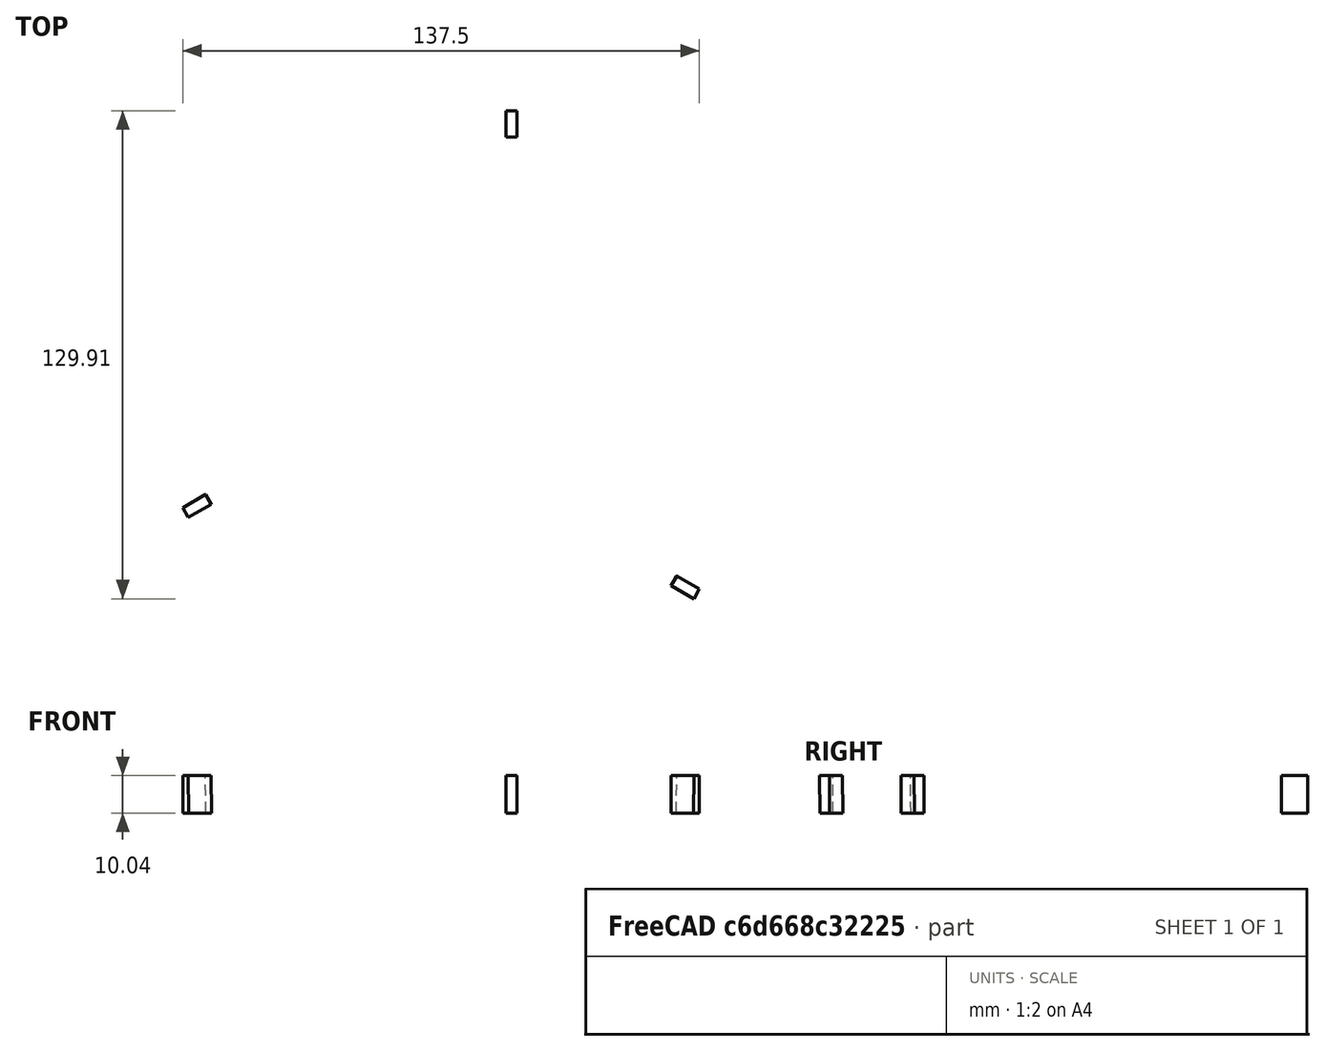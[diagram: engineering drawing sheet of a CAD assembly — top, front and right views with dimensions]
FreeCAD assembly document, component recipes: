
FREECAD ASSEMBLY — COMPONENT RECIPES ("spreadsheet-example-deltarobot")

This assembly document has 17 components, labeled P0..P16 below (a component is one placed body or linked part). 17 of them carry a construction recipe — the FreeCAD feature program that regenerates the part from scratch, quoted from this document or its linked companion documents; the rest are supplied as boundary geometry only. No exploded tour is included for this assembly.
COMPONENT P0 — recipe-attached ("arm", a linked part whose construction recipe lives in a companion FreeCAD document of the same project; that document's serialized recipe follows).
Construction recipe (the companion document, serialized — sketch geometry with constraints, then the solid features built on it; lengths are millimeters unless a unit is written):

FCSTD DOCUMENT  (FreeCAD 2024.1R35694 (Git))
Label: arm
License: All rights reserved
LicenseURL: http://en.wikipedia.org/wiki/All_rights_reserved
objects: Sketcher::SketchObject×11, PartDesign::Pad×6, PartDesign::Plane×2, PartDesign::Revolution×2, PartDesign::Mirrored×2, PartDesign::Body×2, PartDesign::Pocket×2, PartDesign::Chamfer×1, PartDesign::Hole×1, PartDesign::Fillet×1, App::Part×1
note: 43 computed .brp shape members not serialized (recipe doc carries the construction recipe); baked Part::Feature solids carry a one-line shape summary decoded from their .brp

FEATURE [PartDesign::Plane] DatumPlane002  label="midplane001"
  AttachmentOffset = pos=(0,0,7) rot=(0,0,1;0rad)
  Length = 60
  MapMode = 5
  Placement = pos=(0,-7,1.6e-15) rot=(1,0,0;1.5708rad)
  ResizeMode = 0
  Support = -> [XZ_Plane002]
  Width = 60
FEATURE [Sketcher::SketchObject] Sketch008
  FullyConstrained = true
  MapMode = 5
  Placement = pos=(0,0,0) rot=(1,0,0;1.5708rad)
  Support = -> [XZ_Plane002]
  sketch-geometry (5):
    g0: Circle CenterX=0 CenterY=0 CenterZ=0 NormalX=0 NormalY=0 NormalZ=1 AngleXU=0 Radius=2.5
    g1: ArcOfCircle CenterX=0 CenterY=0 CenterZ=0 NormalX=0 NormalY=0 NormalZ=1 AngleXU=0 Radius=6 StartAngle=3.14159 EndAngle=6.28319
    g2: LineSegment StartX=-6 StartY=-1.9e-15 StartZ=0 EndX=-6 EndY=50 EndZ=0
    g3: LineSegment StartX=6 StartY=-1.5e-15 StartZ=0 EndX=6 EndY=50 EndZ=0
    g4: LineSegment StartX=-6 StartY=50 StartZ=0 EndX=6 EndY=50 EndZ=0
  constraints (12):
    c: Coincident(g0,g-1)
    c: Tangent(g1,g2) = 1.5708
    c: Tangent(g1,g3) = -1.5708
    c: Vertical(g3)
    c: Diameter(g0) = 5
    c: Distance(g1,g1) = 12
    c: PointOnObject(g1,g-1)
    c: Coincident(g4,g2)
    c: Coincident(g4,g3)
    c: DistanceY(g3,g3) = 50
    c: Vertical(g2)
    c: Symmetric(g2,g3,g-2)
FEATURE [PartDesign::Pad] Pad003
  Direction = (0,-1,2e-16)
  Length = 8
  Length2 = 10
  Midplane = true
  Placement = pos=(0,0,0) rot=(1,0,0;1.5708rad)
  Profile = -> Sketch008
  ReferenceAxis = -> Sketch008 [N_Axis]
  Type = 0
FEATURE [Sketcher::SketchObject] Sketch009
  FullyConstrained = true
  MapMode = 5
  Placement = pos=(0,0,0) rot=(1,0,0;1.5708rad)
  Support = -> [XZ_Plane002]
  sketch-geometry (2):
    g0: Circle CenterX=0 CenterY=0 CenterZ=0 NormalX=0 NormalY=0 NormalZ=1 AngleXU=0 Radius=2.5
    g1: Circle CenterX=0 CenterY=0 CenterZ=0 NormalX=0 NormalY=0 NormalZ=1 AngleXU=0 Radius=6
  constraints (4):
    c: Coincident(g0,g-1)
    c: Coincident(g1,g0)
    c: Diameter(g0) = 5
    c: Diameter(g1) = 12
FEATURE [PartDesign::Pad] Pad004
  BaseFeature = -> Pad003
  Direction = (0,-1,2e-16)
  Length = 10
  Length2 = 10
  Placement = pos=(0,0,0) rot=(1,0,0;1.5708rad)
  Profile = -> Sketch009
  ReferenceAxis = -> Sketch009 [N_Axis]
  Refine = true
  Type = 0
FEATURE [Sketcher::SketchObject] Sketch010
  ExternalGeometry = -> [Pad004]
  FullyConstrained = true
  MapMode = 5
  Placement = pos=(0,-7,1.6e-15) rot=(1,0,0;1.5708rad)
  Support = -> [DatumPlane002]
  sketch-geometry (4):
    g0: LineSegment StartX=-6 StartY=50 StartZ=0 EndX=6 EndY=50 EndZ=0
    g1: LineSegment StartX=6 StartY=50 StartZ=0 EndX=6 EndY=56 EndZ=0
    g2: LineSegment StartX=6 StartY=56 StartZ=0 EndX=-6 EndY=56 EndZ=0
    g3: LineSegment StartX=-6 StartY=56 StartZ=0 EndX=-6 EndY=50 EndZ=0
  constraints (10):
    c: Coincident(g0,g1)
    c: Coincident(g1,g2)
    c: Coincident(g2,g3)
    c: Coincident(g3,g0)
    c: Horizontal(g2)
    c: Vertical(g1)
    c: Vertical(g3)
    c: Coincident(g0,g-3)
    c: Coincident(g0,g-3)
    c: DistanceY(g1,g1) = 6
FEATURE [PartDesign::Pad] Pad005
  BaseFeature = -> Pad004
  Direction = (0,-1,2e-16)
  Length = 36
  Length2 = 10
  Midplane = true
  Placement = pos=(0,0,0) rot=(1,0,0;1.5708rad)
  Profile = -> Sketch010
  ReferenceAxis = -> Sketch010 [N_Axis]
  Refine = true
  Type = 0
FEATURE [Sketcher::SketchObject] Sketch011
  ExternalGeometry = -> [Pad005,DatumPlane002]
  FullyConstrained = true
  MapMode = 5
  Placement = pos=(0,0,0) rot=(0.57735,0.57735,0.57735;2.0944rad)
  Support = -> [YZ_Plane002]
  sketch-geometry (4):
    g0: LineSegment StartX=-37 StartY=53 StartZ=0 EndX=-25 EndY=53 EndZ=0
    g1: ArcOfCircle CenterX=-32 CenterY=53 CenterZ=0 NormalX=0 NormalY=0 NormalZ=1 AngleXU=0 Radius=5 StartAngle=0.643501 EndAngle=3.14159
    g2: LineSegment StartX=-28 StartY=56 StartZ=0 EndX=-25 EndY=56 EndZ=0
    g3: LineSegment StartX=-25 StartY=56 StartZ=0 EndX=-25 EndY=53 EndZ=0
  constraints (12):
    c: Symmetric(g-3,g-3,g0)
    c: PointOnObject(g1,g0)
    c: Coincident(g1,g0)
    c: PointOnObject(g0,g-3)
    c: Radius(g1) = 5
    c: Distance(g1,g-4) = 25
    c: Coincident(g1,g2)
    c: PointOnObject(g2,g-3)
    c: Horizontal(g2)
    c: Coincident(g2,g3)
    c: Coincident(g3,g0)
    c: DistanceY(g0,g2) = 3
FEATURE [PartDesign::Revolution] Revolution
  Angle = 360
  Angle2 = 60
  Axis = (0,1,0)
  Base = (0,-37,53)
  BaseFeature = -> Pad005
  Placement = pos=(0,0,0) rot=(1,0,0;1.5708rad)
  Profile = -> Sketch011
  ReferenceAxis = -> Sketch011 [Edge1]
  Refine = true
  Type = 0
FEATURE [PartDesign::Mirrored] Mirrored002
  BaseFeature = -> Revolution
  MirrorPlane = -> DatumPlane002
  Originals = -> [Revolution]
  Placement = pos=(0,0,0) rot=(1,0,0;1.5708rad)
  Refine = true
FEATURE [PartDesign::Body] Body001  label="arm-skeleton"
  Group = -> [Sketch008,Pad003,Sketch009,Pad004,DatumPlane002,Sketch010,Pad005,Sketch011,Revolution,Mirrored002]
  Origin = -> Origin002
  Tip = -> Mirrored002
FEATURE [PartDesign::Plane] DatumPlane003  label="midplane002"
  AttachmentOffset = pos=(0,0,7) rot=(0,0,1;0rad)
  Length = 60
  MapMode = 5
  Placement = pos=(0,-7,1.6e-15) rot=(1,0,0;1.5708rad)
  ResizeMode = 0
  Support = -> [XZ_Plane002]
  Width = 60
FEATURE [Sketcher::SketchObject] Sketch012
  FullyConstrained = true
  MapMode = 5
  Placement = pos=(0,0,0) rot=(1,0,0;1.5708rad)
  Support = -> [XZ_Plane003]
  sketch-geometry (5):
    g0: Circle CenterX=0 CenterY=0 CenterZ=0 NormalX=0 NormalY=0 NormalZ=1 AngleXU=0 Radius=2.5
    g1: ArcOfCircle CenterX=0 CenterY=0 CenterZ=0 NormalX=0 NormalY=0 NormalZ=1 AngleXU=0 Radius=6 StartAngle=3.14159 EndAngle=6.28319
    g2: LineSegment StartX=-6 StartY=-1.9e-15 StartZ=0 EndX=-6 EndY=50 EndZ=0
    g3: LineSegment StartX=6 StartY=-1.5e-15 StartZ=0 EndX=6 EndY=50 EndZ=0
    g4: LineSegment StartX=-6 StartY=50 StartZ=0 EndX=6 EndY=50 EndZ=0
  constraints (12):
    c: Coincident(g0,g-1)
    c: Tangent(g1,g2) = 1.5708
    c: Tangent(g1,g3) = -1.5708
    c: Vertical(g3)
    c: Diameter(g0) = 5
    c: Distance(g1,g1) = 12
    c: PointOnObject(g1,g-1)
    c: Coincident(g4,g2)
    c: Coincident(g4,g3)
    c: DistanceY(g3,g3) = 50
    c: Vertical(g2)
    c: Symmetric(g2,g3,g-2)
FEATURE [PartDesign::Pad] Pad006
  Direction = (0,-1,2e-16)
  Length = 8
  Length2 = 10
  Midplane = true
  Placement = pos=(0,0,0) rot=(1,0,0;1.5708rad)
  Profile = -> Sketch012
  ReferenceAxis = -> Sketch012 [N_Axis]
  Type = 0
FEATURE [Sketcher::SketchObject] Sketch013
  FullyConstrained = true
  MapMode = 5
  Placement = pos=(0,0,0) rot=(1,0,0;1.5708rad)
  Support = -> [XZ_Plane003]
  sketch-geometry (2):
    g0: Circle CenterX=0 CenterY=0 CenterZ=0 NormalX=0 NormalY=0 NormalZ=1 AngleXU=0 Radius=2.5
    g1: Circle CenterX=0 CenterY=0 CenterZ=0 NormalX=0 NormalY=0 NormalZ=1 AngleXU=0 Radius=6
  constraints (4):
    c: Coincident(g0,g-1)
    c: Coincident(g1,g0)
    c: Diameter(g0) = 5
    c: Diameter(g1) = 12
FEATURE [PartDesign::Pad] Pad007
  BaseFeature = -> Pad006
  Direction = (0,-1,2e-16)
  Length = 10
  Length2 = 10
  Placement = pos=(0,0,0) rot=(1,0,0;1.5708rad)
  Profile = -> Sketch013
  ReferenceAxis = -> Sketch013 [N_Axis]
  Refine = true
  Type = 0
FEATURE [Sketcher::SketchObject] Sketch014
  ExternalGeometry = -> [Pad007]
  FullyConstrained = true
  MapMode = 5
  Placement = pos=(0,-7,1.6e-15) rot=(1,0,0;1.5708rad)
  Support = -> [DatumPlane003]
  sketch-geometry (4):
    g0: LineSegment StartX=-6 StartY=50 StartZ=0 EndX=6 EndY=50 EndZ=0
    g1: LineSegment StartX=6 StartY=50 StartZ=0 EndX=6 EndY=56 EndZ=0
    g2: LineSegment StartX=6 StartY=56 StartZ=0 EndX=-6 EndY=56 EndZ=0
    g3: LineSegment StartX=-6 StartY=56 StartZ=0 EndX=-6 EndY=50 EndZ=0
  constraints (10):
    c: Coincident(g0,g1)
    c: Coincident(g1,g2)
    c: Coincident(g2,g3)
    c: Coincident(g3,g0)
    c: Horizontal(g2)
    c: Vertical(g1)
    c: Vertical(g3)
    c: Coincident(g0,g-3)
    c: Coincident(g0,g-3)
    c: DistanceY(g1,g1) = 6
FEATURE [PartDesign::Pad] Pad008
  BaseFeature = -> Pad007
  Direction = (0,-1,2e-16)
  Length = 36
  Length2 = 10
  Midplane = true
  Placement = pos=(0,0,0) rot=(1,0,0;1.5708rad)
  Profile = -> Sketch014
  ReferenceAxis = -> Sketch014 [N_Axis]
  Refine = true
  Type = 0
FEATURE [Sketcher::SketchObject] Sketch015
  ExternalGeometry = -> [Pad008,DatumPlane003]
  FullyConstrained = true
  MapMode = 5
  Placement = pos=(0,0,0) rot=(0.57735,0.57735,0.57735;2.0944rad)
  Support = -> [YZ_Plane003]
  sketch-geometry (4):
    g0: LineSegment StartX=-36.9 StartY=53 StartZ=0 EndX=-25 EndY=53 EndZ=0
    g1: ArcOfCircle CenterX=-32 CenterY=53 CenterZ=0 NormalX=0 NormalY=0 NormalZ=1 AngleXU=0 Radius=4.9 StartAngle=0.658897 EndAngle=3.14159
    g2: LineSegment StartX=-28.1257 StartY=56 StartZ=0 EndX=-25 EndY=56 EndZ=0
    g3: LineSegment StartX=-25 StartY=56 StartZ=0 EndX=-25 EndY=53 EndZ=0
  constraints (12):
    c: Symmetric(g-3,g-3,g0)
    c: PointOnObject(g1,g0)
    c: Coincident(g1,g0)
    c: PointOnObject(g0,g-3)
    c: Radius(g1) = 4.9
    c: Distance(g1,g-4) = 25
    c: Coincident(g1,g2)
    c: PointOnObject(g2,g-3)
    c: Horizontal(g2)
    c: Coincident(g2,g3)
    c: Coincident(g3,g0)
    c: DistanceY(g0,g2) = 3
FEATURE [PartDesign::Revolution] Revolution001
  Angle = 360
  Angle2 = 60
  Axis = (0,1,0)
  Base = (0,-36.9,53)
  BaseFeature = -> Pad008
  Placement = pos=(0,0,0) rot=(1,0,0;1.5708rad)
  Profile = -> Sketch015
  ReferenceAxis = -> Sketch015 [Edge1]
  Refine = true
  Type = 0
FEATURE [PartDesign::Mirrored] Mirrored003
  BaseFeature = -> Revolution001
  MirrorPlane = -> DatumPlane003
  Originals = -> [Revolution001]
  Placement = pos=(0,0,0) rot=(1,0,0;1.5708rad)
  Refine = true
FEATURE [PartDesign::Chamfer] Chamfer
  Angle = 45
  Base = -> Mirrored003 [Edge12,Edge10,Edge17,Edge21]
  BaseFeature = -> Mirrored003
  ChamferType = 0
  FlipDirection = false
  Placement = pos=(0,0,0) rot=(1,0,0;1.5708rad)
  Refine = true
  Size = 2
  Size2 = 1
  SupportTransform = false
  UseAllEdges = false
FEATURE [Sketcher::SketchObject] Sketch
  FullyConstrained = true
  MapMode = 5
  Placement = pos=(0,0,0) rot=(1,0,0;1.5708rad)
  Support = -> [XZ_Plane003]
  sketch-geometry (4):
    g0: LineSegment StartX=0.5 StartY=0 StartZ=0 EndX=0.5 EndY=10 EndZ=0
    g1: LineSegment StartX=0.5 StartY=10 StartZ=0 EndX=-0.5 EndY=10 EndZ=0
    g2: LineSegment StartX=-0.5 StartY=10 StartZ=0 EndX=-0.5 EndY=0 EndZ=0
    g3: LineSegment StartX=-0.5 StartY=0 StartZ=0 EndX=0.5 EndY=0 EndZ=0
  constraints (11):
    c: Coincident(g0,g1)
    c: Coincident(g1,g2)
    c: Coincident(g2,g3)
    c: Coincident(g3,g0)
    c: Vertical(g0)
    c: Vertical(g2)
    c: Horizontal(g1)
    c: Horizontal(g3)
    c: Symmetric(g2,g0,g-1)
    c: Distance(g1,g1) = 1
    c: DistanceY(g0,g0) = 10
FEATURE [PartDesign::Pocket] Pocket
  BaseFeature = -> Chamfer
  Direction = (0,1,-2e-16)
  Length = 5
  Length2 = 5
  Midplane = true
  Placement = pos=(0,0,0) rot=(1,0,0;1.5708rad)
  Profile = -> Sketch
  ReferenceAxis = -> Sketch [N_Axis]
  Refine = true
  Type = 1
FEATURE [Sketcher::SketchObject] Sketch016
  FullyConstrained = true
  MapMode = 5
  Placement = pos=(6,0,0) rot=(0.707107,0,0.707107;3.14159rad)
  Support = -> [Pocket]
  sketch-geometry (1):
    g0: Circle CenterX=5 CenterY=0 CenterZ=0 NormalX=0 NormalY=0 NormalZ=1 AngleXU=0 Radius=1.5
  constraints (3):
    c: PointOnObject(g0,g-1)
    c: Diameter(g0) = 3
    c: DistanceX(g-1,g0) = 5
FEATURE [PartDesign::Hole] Hole
  BaseFeature = -> Pocket
  CustomThreadClearance = 0
  Depth = 178.805
  DepthType = 1
  Diameter = 3.4
  DrillForDepth = false
  DrillPoint = 1
  DrillPointAngle = 118
  HoleCutCountersinkAngle = 90
  HoleCutCustomValues = false
  HoleCutDepth = 0
  HoleCutDiameter = 6.1
  HoleCutType = 0
  ModelThread = false
  Placement = pos=(0,0,0) rot=(1,0,0;1.5708rad)
  Profile = -> Sketch016
  Refine = true
  Tapered = false
  TaperedAngle = 90
  ThreadClass = 0
  ThreadDepth = 178.805
  ThreadDepthType = 0
  ThreadDirection = 0
  ThreadFit = 0
  ThreadSize = 9
  ThreadType = 1
  Threaded = false
  UseCustomThreadClearance = false
FEATURE [Sketcher::SketchObject] Sketch017
  ExternalGeometry = -> [Hole]
  FullyConstrained = true
  MapMode = 5
  Placement = pos=(-6,0,0) rot=(0.707107,0,-0.707107;3.14159rad)
  Support = -> [Hole]
  sketch-geometry (7):
    g0: LineSegment StartX=-1.5359 StartY=-4e-16 StartZ=0 EndX=-3.26795 EndY=3 EndZ=0
    g1: LineSegment StartX=-3.26795 StartY=3 StartZ=0 EndX=-6.73205 EndY=3 EndZ=0
    g2: LineSegment StartX=-6.73205 StartY=3 StartZ=0 EndX=-8.4641 EndY=-9e-16 EndZ=0
    g3: LineSegment StartX=-8.4641 StartY=-9e-16 StartZ=0 EndX=-6.73205 EndY=-3 EndZ=0
    g4: LineSegment StartX=-6.73205 StartY=-3 StartZ=0 EndX=-3.26795 EndY=-3 EndZ=0
    g5: LineSegment StartX=-3.26795 StartY=-3 StartZ=0 EndX=-1.5359 EndY=-4e-16 EndZ=0
    g6: Circle CenterX=-5 CenterY=-6e-16 CenterZ=0 NormalX=0 NormalY=0 NormalZ=1 AngleXU=0 Radius=3.4641
  constraints (16):
    c: Coincident(g0,g1)
    c: Coincident(g1,g2)
    c: Coincident(g2,g3)
    c: Coincident(g3,g4)
    c: Coincident(g4,g5)
    c: Coincident(g5,g0)
    c: Equal(g0, g1-g5) x5
    c: PointOnObject(g0,g6)
    c: PointOnObject(g1,g6)
    c: PointOnObject(g2,g6)
    c: PointOnObject(g3,g6)
    c: PointOnObject(g4,g6)
    c: PointOnObject(g5,g6)
    c: Coincident(g6,g-3)
    c: DistanceY(g4,g0) = 6
    c: Horizontal(g1)
FEATURE [PartDesign::Pocket] Pocket001
  BaseFeature = -> Hole
  Direction = (1,0,2e-16)
  Length = 3
  Length2 = 5
  Placement = pos=(0,0,0) rot=(1,0,0;1.5708rad)
  Profile = -> Sketch017
  ReferenceAxis = -> Sketch017 [N_Axis]
  Refine = true
  Type = 0
FEATURE [PartDesign::Fillet] Fillet
  Base = -> Pocket001 [Edge3,Edge46]
  BaseFeature = -> Pocket001
  Placement = pos=(0,0,0) rot=(1,0,0;1.5708rad)
  Radius = 2
  Refine = true
  SupportTransform = false
  UseAllEdges = false
FEATURE [PartDesign::Body] Body002  label="arm0"
  Group = -> [Sketch012,Pad006,Sketch013,Pad007,DatumPlane003,Sketch014,Pad008,Sketch015,Revolution001,Mirrored003,Chamfer,Sketch,Pocket,Sketch016,Hole,Sketch017,Pocket001,Fillet]
  Origin = -> Origin003
  Tip = -> Fillet
FEATURE [App::Part] Part  label="arm"
  Group = -> [Body001,Body002]
  Origin = -> Origin
COMPONENT P1 — same part as P0; its construction recipe is shown at P0.
COMPONENT P2 — same part as P0; its construction recipe is shown at P0.
COMPONENT P3 — recipe-attached ("base 🔒", a linked part whose construction recipe lives in a companion FreeCAD document of the same project; that document's serialized recipe follows).
Construction recipe (the companion document, serialized — sketch geometry with constraints, then the solid features built on it; lengths are millimeters unless a unit is written):

FCSTD DOCUMENT  (FreeCAD 0.22R35451 (Git))
Label: base
License: All rights reserved
LicenseURL: http://en.wikipedia.org/wiki/All_rights_reserved
objects: Sketcher::SketchObject×7, PartDesign::Pad×5, PartDesign::Plane×4, PartDesign::PolarPattern×3, PartDesign::Body×2, PartDesign::Hole×1, PartDesign::Pocket×1, App::Part×1
note: 30 computed .brp shape members not serialized (recipe doc carries the construction recipe); baked Part::Feature solids carry a one-line shape summary decoded from their .brp

FEATURE [PartDesign::Plane] DatumPlane
  Length = 60
  MapMode = 5
  Placement = pos=(0,0,0) rot=(0.57735,0.57735,0.57735;2.0944rad)
  ResizeMode = 0
  Support = -> [YZ_Plane002]
  Width = 60
FEATURE [Sketcher::SketchObject] Sketch001
  FullyConstrained = true
  MapMode = 5
  Placement = pos=(0,0,0) rot=(0.57735,0.57735,0.57735;2.0944rad)
  Support = -> [DatumPlane]
  sketch-geometry (5):
    g0: Circle CenterX=75 CenterY=0 CenterZ=0 NormalX=0 NormalY=0 NormalZ=1 AngleXU=0 Radius=11.25
    g1: LineSegment StartX=96 StartY=21 StartZ=0 EndX=0 EndY=21 EndZ=0
    g2: LineSegment StartX=0 StartY=21 StartZ=0 EndX=0 EndY=-26 EndZ=0
    g3: LineSegment StartX=0 StartY=-26 StartZ=0 EndX=96 EndY=-26 EndZ=0
    g4: LineSegment StartX=96 StartY=-26 StartZ=0 EndX=96 EndY=21 EndZ=0
  constraints (15):
    c: PointOnObject(g0,g-1)
    c: Diameter(g0) = 22.5
    c: DistanceX(g-1,g0) = 75
    c: Coincident(g1,g2)
    c: Coincident(g2,g3)
    c: Coincident(g3,g4)
    c: Coincident(g4,g1)
    c: Horizontal(g1)
    c: Horizontal(g3)
    c: Vertical(g2)
    c: PointOnObject(g2,g-2)
    c: DistanceX(g0,g1) = 21
    c: DistanceY(g-1,g1) = 21
    c: DistanceY(g3,g-1) = 26
    c: Vertical(g4)
FEATURE [PartDesign::Pad] Pad001
  Direction = (1,0,0)
  Length = 5
  Length2 = 10
  Placement = pos=(0,0,0) rot=(0.57735,0.57735,0.57735;2.0944rad)
  Profile = -> Sketch001
  ReferenceAxis = -> Sketch001 [N_Axis]
  Reversed = true
  Type = 0
FEATURE [Sketcher::SketchObject] Sketch002
  ExternalGeometry = -> [Pad001]
  FullyConstrained = true
  MapMode = 5
  Placement = pos=(0,0,0) rot=(0.57735,0.57735,0.57735;2.0944rad)
  Support = -> [Pad001]
  sketch-geometry (5):
    g0: Circle CenterX=90.5 CenterY=15.5 CenterZ=0 NormalX=0 NormalY=0 NormalZ=1 AngleXU=0 Radius=2
    g1: LineSegment StartX=75 StartY=0 StartZ=0 EndX=75 EndY=11.25 EndZ=0
    g2: Circle CenterX=90.5 CenterY=-15.5 CenterZ=0 NormalX=0 NormalY=0 NormalZ=1 AngleXU=0 Radius=2
    g3: Circle CenterX=59.5 CenterY=-15.5 CenterZ=0 NormalX=0 NormalY=0 NormalZ=1 AngleXU=0 Radius=2
    g4: Circle CenterX=59.5 CenterY=15.5 CenterZ=0 NormalX=0 NormalY=0 NormalZ=1 AngleXU=0 Radius=2
  constraints (12):
    c: Coincident(g1,g-3)
    c: PointOnObject(g1,g-3)
    c: Vertical(g1)
    c: Symmetric(g0,g4,g1)
    c: Symmetric(g0,g2,g-1)
    c: Symmetric(g2,g3,g1)
    c: Equal(g4,g0)
    c: Equal(g0,g2)
    c: Equal(g2,g3)
    c: DistanceX(g4,g0) = 31
    c: DistanceY(g2,g0) = 31
    c: Diameter(g0) = 4
FEATURE [PartDesign::Hole] Hole
  BaseFeature = -> Pad001
  CustomThreadClearance = 0
  Depth = 25
  DepthType = 0
  Diameter = 3.4
  DrillForDepth = false
  DrillPoint = 1
  DrillPointAngle = 118
  HoleCutCountersinkAngle = 90
  HoleCutCustomValues = false
  HoleCutDepth = 3.4
  HoleCutDiameter = 6.1
  HoleCutType = 1
  ModelThread = false
  Placement = pos=(0,0,0) rot=(0.57735,0.57735,0.57735;2.0944rad)
  Profile = -> Sketch002
  Tapered = false
  TaperedAngle = 90
  ThreadClass = 0
  ThreadDepth = 25
  ThreadDepthType = 0
  ThreadDirection = 0
  ThreadFit = 0
  ThreadSize = 9
  ThreadType = 1
  Threaded = false
  UseCustomThreadClearance = false
FEATURE [PartDesign::Plane] DatumPlane001
  Length = 60
  MapMode = 5
  Placement = pos=(2.9e-15,0,-26) rot=(0.707107,0.707107,0;3.14159rad)
  ResizeMode = 0
  Support = -> [Pad001]
  Width = 60
FEATURE [Sketcher::SketchObject] Sketch003
  FullyConstrained = true
  MapMode = 5
  Placement = pos=(2.9e-15,0,-26) rot=(0.707107,0.707107,0;3.14159rad)
  Support = -> [DatumPlane001]
  sketch-geometry (1):
    g0: Circle CenterX=0 CenterY=0 CenterZ=0 NormalX=0 NormalY=0 NormalZ=1 AngleXU=0 Radius=5
  constraints (2):
    c: Coincident(g0,g-1)
    c: Diameter(g0) = 10
FEATURE [PartDesign::Pad] Pad002
  BaseFeature = -> Hole
  Direction = (0,0,-1)
  Length = 42
  Length2 = 10
  Placement = pos=(0,0,0) rot=(0.57735,0.57735,0.57735;2.0944rad)
  Profile = -> Sketch003
  ReferenceAxis = -> Sketch003 [N_Axis]
  Refine = true
  Reversed = true
  Type = 1
FEATURE [PartDesign::PolarPattern] PolarPattern
  Angle = 360
  Axis = -> Z_Axis002
  BaseFeature = -> Pad002
  Mode = 0
  Occurrences = 3
  Offset = 120
  Originals = -> [Pad001,Hole]
  Placement = pos=(0,0,0) rot=(0.57735,0.57735,0.57735;2.0944rad)
  Refine = true
FEATURE [Sketcher::SketchObject] Sketch
  FullyConstrained = true
  MapMode = 5
  Placement = pos=(2.9e-15,0,-26) rot=(0.707107,0.707107,0;3.14159rad)
  Support = -> [DatumPlane001]
  sketch-geometry (8):
    g0: LineSegment StartX=96 StartY=0 StartZ=0 EndX=-48 EndY=83.1384 EndZ=0
    g1: LineSegment StartX=-48 StartY=83.1384 StartZ=0 EndX=-48 EndY=-83.1384 EndZ=0
    g2: LineSegment StartX=-48 StartY=-83.1384 StartZ=0 EndX=96 EndY=0 EndZ=0
    g3: Circle CenterX=0 CenterY=0 CenterZ=0 NormalX=0 NormalY=0 NormalZ=1 AngleXU=0 Radius=96
    g4: LineSegment StartX=60 StartY=0 StartZ=0 EndX=-30 EndY=51.9615 EndZ=0
    g5: LineSegment StartX=-30 StartY=51.9615 StartZ=0 EndX=-30 EndY=-51.9615 EndZ=0
    g6: LineSegment StartX=-30 StartY=-51.9615 StartZ=0 EndX=60 EndY=0 EndZ=0
    g7: Circle CenterX=0 CenterY=0 CenterZ=0 NormalX=0 NormalY=0 NormalZ=1 AngleXU=0 Radius=60
  constraints (22):
    c: Coincident(g0,g1)
    c: Coincident(g1,g2)
    c: Coincident(g2,g0)
    c: Equal(g0,g1)
    c: Equal(g0,g2)
    c: PointOnObject(g0,g3)
    c: PointOnObject(g1,g3)
    c: PointOnObject(g2,g3)
    c: Coincident(g3,g-1)
    c: PointOnObject(g2,g-1)
    c: Coincident(g4,g5)
    c: Coincident(g5,g6)
    c: Coincident(g6,g4)
    c: Equal(g4,g5)
    c: Equal(g4,g6)
    c: PointOnObject(g4,g7)
    c: PointOnObject(g5,g7)
    c: PointOnObject(g6,g7)
    c: Coincident(g7,g3)
    c: PointOnObject(g6,g-1)
    c: DistanceX(g-1,g0) = 96
    c: DistanceX(g-1,g4) = 60
FEATURE [PartDesign::Pad] Pad
  BaseFeature = -> PolarPattern
  Direction = (0,0,-1)
  Length = 4
  Length2 = 10
  Placement = pos=(0,0,0) rot=(0.57735,0.57735,0.57735;2.0944rad)
  Profile = -> Sketch
  ReferenceAxis = -> Sketch [N_Axis]
  Refine = true
  Reversed = true
  Type = 0
FEATURE [Sketcher::SketchObject] Sketch004
  ExternalGeometry = -> [Pad]
  FullyConstrained = true
  MapMode = 5
  Placement = pos=(0,0,0) rot=(0.57735,0.57735,0.57735;2.0944rad)
  Support = -> [YZ_Plane002]
  sketch-geometry (4):
    g0: LineSegment StartX=82 StartY=21 StartZ=0 EndX=68 EndY=21 EndZ=0
    g1: LineSegment StartX=68 StartY=21 StartZ=0 EndX=68 EndY=8.80696 EndZ=0
    g2: LineSegment StartX=68 StartY=8.80696 StartZ=0 EndX=82 EndY=8.80696 EndZ=0
    g3: LineSegment StartX=82 StartY=8.80696 StartZ=0 EndX=82 EndY=21 EndZ=0
  constraints (12):
    c: Coincident(g0,g1)
    c: Coincident(g1,g2)
    c: Coincident(g2,g3)
    c: Coincident(g3,g0)
    c: Horizontal(g0)
    c: Horizontal(g2)
    c: Vertical(g1)
    c: Vertical(g3)
    c: PointOnObject(g0,g-4)
    c: PointOnObject(g1,g-3)
    c: PointOnObject(g2,g-3)
    c: DistanceX(g0,g0) = 14
FEATURE [PartDesign::Pocket] Pocket
  BaseFeature = -> Pad
  Direction = (-1,0,0)
  Length = 5
  Length2 = 5
  Placement = pos=(0,0,0) rot=(0.57735,0.57735,0.57735;2.0944rad)
  Profile = -> Sketch004
  ReferenceAxis = -> Sketch004 [N_Axis]
  Refine = true
  Type = 0
FEATURE [PartDesign::PolarPattern] PolarPattern001
  Angle = 360
  Axis = -> Z_Axis002
  BaseFeature = -> Pocket
  Mode = 0
  Occurrences = 3
  Offset = 120
  Originals = -> [Pocket]
  Placement = pos=(0,0,0) rot=(0.57735,0.57735,0.57735;2.0944rad)
  Refine = true
FEATURE [PartDesign::Body] Body001  label="base0"
  Group = -> [DatumPlane,Sketch001,Pad001,DatumPlane001,Sketch002,Hole,Sketch003,Pad002,PolarPattern,Sketch,Pad,Sketch004,Pocket,PolarPattern001]
  Origin = -> Origin002
  Tip = -> PolarPattern001
FEATURE [PartDesign::Plane] DatumPlane002
  Length = 60
  MapMode = 5
  Placement = pos=(0,0,0) rot=(0.57735,0.57735,0.57735;2.0944rad)
  ResizeMode = 0
  Support = -> [YZ_Plane003]
  Width = 60
FEATURE [Sketcher::SketchObject] Sketch006
  FullyConstrained = true
  MapMode = 5
  Placement = pos=(0,0,0) rot=(0.57735,0.57735,0.57735;2.0944rad)
  Support = -> [DatumPlane002]
  sketch-geometry (5):
    g0: Circle CenterX=75 CenterY=0 CenterZ=0 NormalX=0 NormalY=0 NormalZ=1 AngleXU=0 Radius=11.25
    g1: LineSegment StartX=96 StartY=21 StartZ=0 EndX=0 EndY=21 EndZ=0
    g2: LineSegment StartX=0 StartY=21 StartZ=0 EndX=0 EndY=-26 EndZ=0
    g3: LineSegment StartX=0 StartY=-26 StartZ=0 EndX=96 EndY=-26 EndZ=0
    g4: LineSegment StartX=96 StartY=-26 StartZ=0 EndX=96 EndY=21 EndZ=0
  constraints (15):
    c: PointOnObject(g0,g-1)
    c: Diameter(g0) = 22.5
    c: DistanceX(g-1,g0) = 75
    c: Coincident(g1,g2)
    c: Coincident(g2,g3)
    c: Coincident(g3,g4)
    c: Coincident(g4,g1)
    c: Horizontal(g1)
    c: Horizontal(g3)
    c: Vertical(g2)
    c: PointOnObject(g2,g-2)
    c: DistanceX(g0,g1) = 21
    c: DistanceY(g-1,g1) = 21
    c: DistanceY(g3,g-1) = 26
    c: Vertical(g4)
FEATURE [PartDesign::Pad] Pad004
  Direction = (1,0,0)
  Length = 5
  Length2 = 10
  Placement = pos=(0,0,0) rot=(0.57735,0.57735,0.57735;2.0944rad)
  Profile = -> Sketch006
  ReferenceAxis = -> Sketch006 [N_Axis]
  Reversed = true
  Type = 0
FEATURE [PartDesign::Plane] DatumPlane003
  Length = 60
  MapMode = 5
  Placement = pos=(2.9e-15,0,-26) rot=(0.707107,0.707107,0;3.14159rad)
  ResizeMode = 0
  Support = -> [Pad004]
  Width = 60
FEATURE [Sketcher::SketchObject] Sketch008
  FullyConstrained = true
  MapMode = 5
  Placement = pos=(2.9e-15,0,-26) rot=(0.707107,0.707107,0;3.14159rad)
  Support = -> [DatumPlane003]
  sketch-geometry (1):
    g0: Circle CenterX=0 CenterY=0 CenterZ=0 NormalX=0 NormalY=0 NormalZ=1 AngleXU=0 Radius=5
  constraints (2):
    c: Coincident(g0,g-1)
    c: Diameter(g0) = 10
FEATURE [PartDesign::Pad] Pad005
  BaseFeature = -> Pad004
  Direction = (0,0,-1)
  Length = 42
  Length2 = 10
  Placement = pos=(0,0,0) rot=(0.57735,0.57735,0.57735;2.0944rad)
  Profile = -> Sketch008
  ReferenceAxis = -> Sketch008 [N_Axis]
  Refine = true
  Reversed = true
  Type = 1
FEATURE [PartDesign::PolarPattern] PolarPattern002
  Angle = 360
  Axis = -> Z_Axis003
  BaseFeature = -> Pad005
  Mode = 0
  Occurrences = 3
  Offset = 120
  Originals = -> [Pad004]
  Placement = pos=(0,0,0) rot=(0.57735,0.57735,0.57735;2.0944rad)
  Refine = true
FEATURE [PartDesign::Body] Body002  label="base-skeleton"
  Group = -> [DatumPlane002,Sketch006,Pad004,DatumPlane003,Sketch008,Pad005,PolarPattern002]
  Origin = -> Origin003
  Tip = -> PolarPattern002
FEATURE [App::Part] Part  label="base"
  Group = -> [Body002,Body001]
  Origin = -> Origin
COMPONENT P4 — recipe-attached ("cone", a linked part whose construction recipe lives in a companion FreeCAD document of the same project; that document's serialized recipe follows).
Construction recipe (the companion document, serialized — sketch geometry with constraints, then the solid features built on it; lengths are millimeters unless a unit is written):

FCSTD DOCUMENT  (FreeCAD 0.22R35451 (Git))
Label: cone
License: All rights reserved
LicenseURL: http://en.wikipedia.org/wiki/All_rights_reserved
objects: Sketcher::SketchObject×1, PartDesign::Revolution×1, PartDesign::Body×1, App::Part×1
note: 4 computed .brp shape members not serialized (recipe doc carries the construction recipe); baked Part::Feature solids carry a one-line shape summary decoded from their .brp

FEATURE [Sketcher::SketchObject] Sketch
  FullyConstrained = true
  MapMode = 5
  Placement = pos=(0,0,0) rot=(1,0,0;1.5708rad)
  Support = -> [XZ_Plane001]
  sketch-geometry (4):
    g0: LineSegment StartX=0 StartY=0 StartZ=0 EndX=0 EndY=20 EndZ=0
    g1: LineSegment StartX=0 StartY=20 StartZ=0 EndX=2 EndY=20 EndZ=0
    g2: ArcOfCircle CenterX=31 CenterY=20 CenterZ=0 NormalX=0 NormalY=0 NormalZ=1 AngleXU=0 Radius=29 StartAngle=3.14159 EndAngle=3.90261
    g3: LineSegment StartX=10 StartY=0 StartZ=0 EndX=0 EndY=0 EndZ=0
  constraints (11):
    c: Coincident(g-1,g0)
    c: PointOnObject(g0,g-2)
    c: Coincident(g0,g1)
    c: Horizontal(g1)
    c: Perpendicular(g1,g2) = 4.71239
    c: PointOnObject(g2,g-1)
    c: Coincident(g2,g3)
    c: Coincident(g3,g0)
    c: DistanceX(g1,g1) = 2
    c: DistanceX(g3,g3) = 10
    c: DistanceY(g0,g0) = 20
FEATURE [PartDesign::Revolution] Revolution
  Angle = 360
  Angle2 = 60
  Axis = (0,2e-16,1)
  Base = (0,0,0)
  Placement = pos=(0,0,0) rot=(1,0,0;1.5708rad)
  Profile = -> Sketch
  ReferenceAxis = -> Sketch [V_Axis]
  Refine = true
  Reversed = true
  Type = 0
FEATURE [PartDesign::Body] Body  label="cone0"
  Group = -> [Sketch,Revolution]
  Origin = -> Origin001
  Tip = -> Revolution
FEATURE [App::Part] Part  label="cone"
  Group = -> [Body]
  Origin = -> Origin
COMPONENT P5 — same part as P4; its construction recipe is shown at P4.
COMPONENT P6 — same part as P4; its construction recipe is shown at P4.
COMPONENT P7 — recipe-attached ("link", a linked part whose construction recipe lives in a companion FreeCAD document of the same project; that document's serialized recipe follows).
Construction recipe (the companion document, serialized — sketch geometry with constraints, then the solid features built on it; lengths are millimeters unless a unit is written):

FCSTD DOCUMENT  (FreeCAD 0.22R35451 (Git))
Label: link
License: All rights reserved
LicenseURL: http://en.wikipedia.org/wiki/All_rights_reserved
objects: Sketcher::SketchObject×5, PartDesign::Pad×2, PartDesign::Groove×2, PartDesign::Mirrored×2, PartDesign::Body×2, PartDesign::Pocket×1, PartDesign::Fillet×1, App::Part×1
note: 21 computed .brp shape members not serialized (recipe doc carries the construction recipe); baked Part::Feature solids carry a one-line shape summary decoded from their .brp

FEATURE [Sketcher::SketchObject] Sketch
  FullyConstrained = true
  MapMode = 5
  Support = -> [XY_Plane001]
  sketch-geometry (4):
    g0: ArcOfCircle CenterX=-70 CenterY=0 CenterZ=0 NormalX=0 NormalY=0 NormalZ=1 AngleXU=0 Radius=8 StartAngle=0.384397 EndAngle=5.89879
    g1: ArcOfCircle CenterX=70 CenterY=0 CenterZ=0 NormalX=0 NormalY=0 NormalZ=1 AngleXU=0 Radius=8 StartAngle=3.52599 EndAngle=9.04038
    g2: LineSegment StartX=-62.5838 StartY=-3 StartZ=0 EndX=62.5838 EndY=-3 EndZ=0
    g3: LineSegment StartX=62.5838 StartY=3 StartZ=0 EndX=-62.5838 EndY=3 EndZ=0
  constraints (13):
    c: PointOnObject(g0,g-1)
    c: Symmetric(g0,g1,g-1)
    c: Equal(g0,g1)
    c: DistanceX(g0,g1) = 140
    c: Horizontal(g2)
    c: Horizontal(g3)
    c: Coincident(g0,g3)
    c: Coincident(g1,g2)
    c: Coincident(g2,g0)
    c: Vertical(g0,g0)
    c: Radius(g0) = 8
    c: Distance(g0,g0) = 6
    c: Coincident(g1,g3)
FEATURE [PartDesign::Pad] Pad
  Direction = (0,0,1)
  Length = 6
  Length2 = 4
  Midplane = true
  Profile = -> Sketch
  ReferenceAxis = -> Sketch [N_Axis]
  Refine = true
  Type = 4
FEATURE [Sketcher::SketchObject] Sketch001
  FullyConstrained = true
  MapMode = 5
  Placement = pos=(0,0,0) rot=(1,0,0;1.5708rad)
  Support = -> [XZ_Plane001]
  sketch-geometry (4):
    g0: ArcOfCircle CenterX=-70 CenterY=0 CenterZ=0 NormalX=0 NormalY=0 NormalZ=1 AngleXU=0 Radius=5 StartAngle=1.5708 EndAngle=3.54431
    g1: LineSegment StartX=-74.6 StartY=-1.95959 StartZ=0 EndX=-79.2421 EndY=-10 EndZ=0
    g2: LineSegment StartX=-79.2421 StartY=-10 StartZ=0 EndX=-70 EndY=-10 EndZ=0
    g3: LineSegment StartX=-70 StartY=5 StartZ=0 EndX=-70 EndY=-10 EndZ=0
  constraints (13):
    c: Coincident(g1,g2)
    c: Horizontal(g2)
    c: PointOnObject(g0,g-1)
    c: Coincident(g3,g0)
    c: Coincident(g3,g2)
    c: Vertical(g3)
    c: PointOnObject(g0,g3)
    c: Radius(g0) = 5
    c: DistanceX(g0,g2) = 4.6
    c: DistanceX(g0,g-1) = 70
    c: Angle(g1,g3) = 0.523599
    c: DistanceY(g3,g3) = 15
    c: Coincident(g1,g0)
FEATURE [PartDesign::Groove] Groove
  Angle = 360
  Angle2 = 60
  Axis = (0,-2e-16,-1)
  Base = (-70,1.1e-15,5)
  BaseFeature = -> Pad
  Profile = -> Sketch001
  ReferenceAxis = -> Sketch001 [Edge4]
  Refine = true
  Reversed = true
  Type = 0
FEATURE [Sketcher::SketchObject] Sketch003
  FullyConstrained = true
  MapMode = 5
  Support = -> [XY_Plane002]
  sketch-geometry (4):
    g0: ArcOfCircle CenterX=-70 CenterY=0 CenterZ=0 NormalX=0 NormalY=0 NormalZ=1 AngleXU=0 Radius=8 StartAngle=0.384397 EndAngle=5.89879
    g1: ArcOfCircle CenterX=70 CenterY=0 CenterZ=0 NormalX=0 NormalY=0 NormalZ=1 AngleXU=0 Radius=8 StartAngle=3.52599 EndAngle=9.04038
    g2: LineSegment StartX=-62.5838 StartY=-3 StartZ=0 EndX=62.5838 EndY=-3 EndZ=0
    g3: LineSegment StartX=62.5838 StartY=3 StartZ=0 EndX=-62.5838 EndY=3 EndZ=0
  constraints (13):
    c: PointOnObject(g0,g-1)
    c: Symmetric(g0,g1,g-1)
    c: Equal(g0,g1)
    c: DistanceX(g0,g1) = 140
    c: Horizontal(g2)
    c: Horizontal(g3)
    c: Coincident(g0,g3)
    c: Coincident(g1,g2)
    c: Coincident(g2,g0)
    c: Vertical(g0,g0)
    c: Radius(g0) = 8
    c: Distance(g0,g0) = 6
    c: Coincident(g1,g3)
FEATURE [PartDesign::Pad] Pad001
  Direction = (0,0,1)
  Length = 6
  Length2 = 4
  Midplane = true
  Profile = -> Sketch003
  ReferenceAxis = -> Sketch003 [N_Axis]
  Refine = true
  Type = 4
FEATURE [Sketcher::SketchObject] Sketch004
  FullyConstrained = true
  MapMode = 5
  Placement = pos=(0,0,0) rot=(1,0,0;1.5708rad)
  Support = -> [XZ_Plane001]
  sketch-geometry (4):
    g0: ArcOfCircle CenterX=-70 CenterY=0 CenterZ=0 NormalX=0 NormalY=0 NormalZ=1 AngleXU=0 Radius=5 StartAngle=1.5708 EndAngle=3.54431
    g1: LineSegment StartX=-74.6 StartY=-1.95959 StartZ=0 EndX=-79.2421 EndY=-10 EndZ=0
    g2: LineSegment StartX=-79.2421 StartY=-10 StartZ=0 EndX=-70 EndY=-10 EndZ=0
    g3: LineSegment StartX=-70 StartY=5 StartZ=0 EndX=-70 EndY=-10 EndZ=0
  constraints (13):
    c: Coincident(g1,g2)
    c: Horizontal(g2)
    c: PointOnObject(g0,g-1)
    c: Coincident(g3,g0)
    c: Coincident(g3,g2)
    c: Vertical(g3)
    c: PointOnObject(g0,g3)
    c: Radius(g0) = 5
    c: DistanceX(g0,g2) = 4.6
    c: DistanceX(g0,g-1) = 70
    c: Angle(g1,g3) = 0.523599
    c: DistanceY(g3,g3) = 15
    c: Coincident(g1,g0)
FEATURE [PartDesign::Groove] Groove001
  Angle = 360
  Angle2 = 60
  Axis = (0,-2e-16,-1)
  Base = (-70,1.1e-15,5)
  BaseFeature = -> Pad001
  Profile = -> Sketch004
  ReferenceAxis = -> Sketch004 [Edge4]
  Refine = true
  Reversed = true
  Type = 0
FEATURE [Sketcher::SketchObject] Sketch005
  ExternalGeometry = -> [Sketch004]
  FullyConstrained = true
  MapMode = 5
  Placement = pos=(0,0,-4) rot=(1,0,0;3.14159rad)
  Support = -> [Groove001]
  sketch-geometry (4):
    g0: LineSegment StartX=-71 StartY=0.5 StartZ=0 EndX=-81 EndY=0.5 EndZ=0
    g1: LineSegment StartX=-81 StartY=0.5 StartZ=0 EndX=-81 EndY=-0.5 EndZ=0
    g2: LineSegment StartX=-81 StartY=-0.5 StartZ=0 EndX=-71 EndY=-0.5 EndZ=0
    g3: LineSegment StartX=-71 StartY=-0.5 StartZ=0 EndX=-71 EndY=0.5 EndZ=0
  constraints (11):
    c: Coincident(g0,g1)
    c: Coincident(g1,g2)
    c: Coincident(g2,g3)
    c: Coincident(g3,g0)
    c: Horizontal(g0)
    c: Horizontal(g2)
    c: Vertical(g1)
    c: Symmetric(g2,g0,g-1)
    c: Distance(g3,g3) = 1
    c: DistanceX(g2,g-3) = 1
    c: DistanceX(g2,g2) = 10
FEATURE [PartDesign::Pocket] Pocket
  BaseFeature = -> Groove001
  Direction = (0,0,1)
  Length = 8
  Length2 = 5
  Profile = -> Sketch005
  ReferenceAxis = -> Sketch005 [N_Axis]
  Refine = true
  Type = 0
FEATURE [PartDesign::Mirrored] Mirrored
  BaseFeature = -> Groove
  MirrorPlane = -> Sketch001 [V_Axis]
  Originals = -> [Groove]
  Refine = true
FEATURE [PartDesign::Body] Body  label="link-skel"
  Group = -> [Sketch,Pad,Sketch001,Groove,Mirrored]
  Origin = -> Origin001
  Tip = -> Mirrored
FEATURE [PartDesign::Mirrored] Mirrored001
  BaseFeature = -> Pocket
  MirrorPlane = -> Sketch005 [V_Axis]
  Originals = -> [Pocket,Groove001]
  Refine = true
FEATURE [PartDesign::Fillet] Fillet
  Base = -> Mirrored001 [Edge6,Edge8,Edge31,Edge27]
  BaseFeature = -> Mirrored001
  Radius = 10
  Refine = true
  SupportTransform = false
  UseAllEdges = false
FEATURE [PartDesign::Body] Body001  label="link0"
  Group = -> [Sketch003,Pad001,Sketch004,Groove001,Sketch005,Pocket,Mirrored001,Fillet]
  Origin = -> Origin002
  Tip = -> Fillet
FEATURE [App::Part] Part  label="link"
  Group = -> [Body,Body001]
  Origin = -> Origin
COMPONENT P8 — same part as P7; its construction recipe is shown at P7.
COMPONENT P9 — same part as P7; its construction recipe is shown at P7.
COMPONENT P10 — same part as P7; its construction recipe is shown at P7.
COMPONENT P11 — same part as P7; its construction recipe is shown at P7.
COMPONENT P12 — same part as P7; its construction recipe is shown at P7.
COMPONENT P13 — recipe-attached ("nema17_049", a linked part whose construction recipe lives in a companion FreeCAD document of the same project; that document's serialized recipe follows).
Construction recipe (the companion document, serialized — sketch geometry with constraints, then the solid features built on it; lengths are millimeters unless a unit is written):

FCSTD DOCUMENT  (FreeCAD 0.22R35451 (Git))
Label: nema17-48
License: All rights reserved
LicenseURL: http://en.wikipedia.org/wiki/All_rights_reserved
objects: Sketcher::SketchObject×4, PartDesign::Pad×3, PartDesign::Chamfer×2, PartDesign::Hole×1, PartDesign::Body×1, App::Part×1
note: 17 computed .brp shape members not serialized (recipe doc carries the construction recipe); baked Part::Feature solids carry a one-line shape summary decoded from their .brp

FEATURE [Sketcher::SketchObject] Sketch
  FullyConstrained = false
  MapMode = 5
  Support = -> [XY_Plane]
  sketch-geometry (5):
    g0: LineSegment StartX=21.15 StartY=21.15 StartZ=0 EndX=-21.15 EndY=21.15 EndZ=0
    g1: LineSegment StartX=-21.15 StartY=21.15 StartZ=0 EndX=-21.15 EndY=-21.15 EndZ=0
    g2: LineSegment StartX=-21.15 StartY=-21.15 StartZ=0 EndX=21.15 EndY=-21.15 EndZ=0
    g3: LineSegment StartX=21.15 StartY=-21.15 StartZ=0 EndX=21.15 EndY=21.15 EndZ=0
    g4: Circle CenterX=0 CenterY=0 CenterZ=0 NormalX=0 NormalY=0 NormalZ=1 AngleXU=0 Radius=29.9106
  constraints (14):
    c: Coincident(g0,g1)
    c: Coincident(g1,g2)
    c: Coincident(g2,g3)
    c: Coincident(g3,g0)
    c: Equal(g0,g1)
    c: Equal(g0,g2)
    c: Equal(g0,g3)
    c: PointOnObject(g0,g4)
    c: PointOnObject(g1,g4)
    c: PointOnObject(g2,g4)
    c: PointOnObject(g3,g4)
    c: Coincident(g4,g-1)
    c: Horizontal(g0)
    c: DistanceY(g3,g3) = 42.3
FEATURE [PartDesign::Pad] Pad
  Direction = (0,0,1)
  Length = 48
  Length2 = 100
  Profile = -> Sketch
  ReferenceAxis = -> Sketch [N_Axis]
  Type = 0
FEATURE [Sketcher::SketchObject] Sketch001
  FullyConstrained = true
  MapMode = 5
  Placement = pos=(0,0,48) rot=(0,0,1;0rad)
  Support = -> [Pad]
  sketch-geometry (1):
    g0: Circle CenterX=0 CenterY=0 CenterZ=0 NormalX=0 NormalY=0 NormalZ=1 AngleXU=0 Radius=11
  constraints (2):
    c: Coincident(g0,g-1)
    c: Diameter(g0) = 22
FEATURE [PartDesign::Pad] Pad001
  BaseFeature = -> Pad
  Direction = (0,0,1)
  Length = 2
  Length2 = 100
  Profile = -> Sketch001
  ReferenceAxis = -> Sketch001 [N_Axis]
  Type = 0
FEATURE [Sketcher::SketchObject] Sketch002
  FullyConstrained = true
  MapMode = 5
  Placement = pos=(0,0,48) rot=(0,0,1;0rad)
  Support = -> [Pad001]
  sketch-geometry (1):
    g0: Circle CenterX=0 CenterY=0 CenterZ=0 NormalX=0 NormalY=0 NormalZ=1 AngleXU=0 Radius=2.5
  constraints (2):
    c: Coincident(g0,g-1)
    c: Diameter(g0) = 5
FEATURE [PartDesign::Pad] Pad002
  BaseFeature = -> Pad001
  Direction = (0,0,1)
  Length = 24
  Length2 = 100
  Profile = -> Sketch002
  ReferenceAxis = -> Sketch002 [N_Axis]
  Type = 0
FEATURE [PartDesign::Chamfer] Chamfer
  Angle = 45
  Base = -> Pad002 [Edge18]
  BaseFeature = -> Pad002
  ChamferType = 0
  FlipDirection = false
  Size = 0.5
  Size2 = 1
  SupportTransform = true
  UseAllEdges = false
FEATURE [Sketcher::SketchObject] Sketch004
  FullyConstrained = true
  MapMode = 5
  Placement = pos=(0,0,48) rot=(0,0,1;0rad)
  sketch-geometry (4):
    g0: Circle CenterX=15.5 CenterY=-15.5 CenterZ=0 NormalX=0 NormalY=0 NormalZ=1 AngleXU=0 Radius=1.25
    g1: Circle CenterX=15.5 CenterY=15.5 CenterZ=0 NormalX=0 NormalY=0 NormalZ=1 AngleXU=0 Radius=1.25
    g2: Circle CenterX=-15.5 CenterY=15.5 CenterZ=0 NormalX=0 NormalY=0 NormalZ=1 AngleXU=0 Radius=1.25
    g3: Circle CenterX=-15.5 CenterY=-15.5 CenterZ=0 NormalX=0 NormalY=0 NormalZ=1 AngleXU=0 Radius=1.25
  constraints (9):
    c: Diameter(g0) = 2.5
    c: Symmetric(g1,g0,g-1)
    c: Symmetric(g1,g2,g-2)
    c: Symmetric(g3,g2,g-1)
    c: Equal(g2,g1)
    c: Equal(g1,g3)
    c: Equal(g3,g0)
    c: DistanceX(g2,g1) = 31
    c: DistanceY(g0,g1) = 31
FEATURE [PartDesign::Hole] Hole
  BaseFeature = -> Chamfer
  CustomThreadClearance = 0
  Depth = 4
  DepthType = 0
  Diameter = 3.4
  DrillForDepth = false
  DrillPoint = 1
  DrillPointAngle = 118
  HoleCutCountersinkAngle = 90
  HoleCutCustomValues = false
  HoleCutDepth = 0
  HoleCutDiameter = 1.6
  HoleCutType = 0
  ModelThread = false
  Profile = -> Sketch004
  Tapered = false
  TaperedAngle = 90
  ThreadClass = 0
  ThreadDepth = 4
  ThreadDepthType = 0
  ThreadDirection = 0
  ThreadFit = 0
  ThreadSize = 9
  ThreadType = 1
  Threaded = false
  UseCustomThreadClearance = false
FEATURE [PartDesign::Chamfer] Chamfer001
  Angle = 45
  Base = -> Hole [Edge20,Edge17,Edge22,Edge18]
  BaseFeature = -> Hole
  ChamferType = 0
  FlipDirection = false
  Size = 5
  Size2 = 1
  SupportTransform = true
  UseAllEdges = false
FEATURE [PartDesign::Body] Body  label="nema17"
  Group = -> [Sketch,Pad,Sketch001,Pad001,Sketch002,Pad002,Chamfer,Sketch004,Hole,Chamfer001]
  Origin = -> Origin
  Placement = pos=(0,0,-50) rot=(0,0,1;0rad)
  Tip = -> Chamfer001
FEATURE [App::Part] Part  label="nema17-48"
  Group = -> [Body]
  Origin = -> Origin001
COMPONENT P14 — same part as P13; its construction recipe is shown at P13.
COMPONENT P15 — same part as P13; its construction recipe is shown at P13.
COMPONENT P16 — recipe-attached ("plate 🔒", a linked part whose construction recipe lives in a companion FreeCAD document of the same project; that document's serialized recipe follows).
Construction recipe (the companion document, serialized — sketch geometry with constraints, then the solid features built on it; lengths are millimeters unless a unit is written):

FCSTD DOCUMENT  (FreeCAD 2024.1R35694 (Git))
Label: plate
License: All rights reserved
LicenseURL: http://en.wikipedia.org/wiki/All_rights_reserved
objects: Sketcher::SketchObject×6, PartDesign::PolarPattern×3, PartDesign::Pad×2, PartDesign::Revolution×2, PartDesign::Body×2, PartDesign::Chamfer×2, PartDesign::Pocket×2, App::Part×1
note: 27 computed .brp shape members not serialized (recipe doc carries the construction recipe); baked Part::Feature solids carry a one-line shape summary decoded from their .brp

FEATURE [Sketcher::SketchObject] Sketch003
  FullyConstrained = true
  MapMode = 5
  Support = -> [XY_Plane002]
  sketch-geometry (4):
    g0: LineSegment StartX=19 StartY=0 StartZ=0 EndX=19 EndY=50 EndZ=0
    g1: LineSegment StartX=19 StartY=50 StartZ=0 EndX=-19 EndY=50 EndZ=0
    g2: LineSegment StartX=-19 StartY=50 StartZ=0 EndX=-19 EndY=0 EndZ=0
    g3: LineSegment StartX=-19 StartY=0 StartZ=0 EndX=19 EndY=0 EndZ=0
  constraints (11):
    c: Coincident(g0,g1)
    c: Coincident(g1,g2)
    c: Coincident(g2,g3)
    c: Coincident(g3,g0)
    c: Vertical(g0)
    c: Vertical(g2)
    c: Horizontal(g1)
    c: PointOnObject(g0,g-1)
    c: Symmetric(g2,g0,g-2)
    c: DistanceX(g3,g3) = 38
    c: DistanceY(g0,g0) = 50
FEATURE [PartDesign::Pad] Pad001
  Direction = (0,0,1)
  Length = 6
  Length2 = 10
  Profile = -> Sketch003
  ReferenceAxis = -> Sketch003 [N_Axis]
  Type = 0
FEATURE [Sketcher::SketchObject] Sketch
  ExternalGeometry = -> [Pad001]
  FullyConstrained = true
  MapMode = 5
  Support = -> [XY_Plane002]
  sketch-geometry (4):
    g0: LineSegment StartX=-30 StartY=50 StartZ=0 EndX=30 EndY=50 EndZ=0
    g1: ArcOfCircle CenterX=-25 CenterY=50 CenterZ=0 NormalX=0 NormalY=0 NormalZ=1 AngleXU=0 Radius=5 StartAngle=0.643501 EndAngle=3.14159
    g2: ArcOfCircle CenterX=25 CenterY=50 CenterZ=0 NormalX=0 NormalY=0 NormalZ=1 AngleXU=0 Radius=5 StartAngle=-9e-16 EndAngle=2.49809
    g3: LineSegment StartX=-21 StartY=53 StartZ=0 EndX=21 EndY=53 EndZ=0
  constraints (12):
    c: Symmetric(g0,g0,g-2)
    c: PointOnObject(g-3,g0)
    c: PointOnObject(g1,g0)
    c: Coincident(g1,g0)
    c: Coincident(g2,g0)
    c: Symmetric(g1,g2,g-2)
    c: DistanceX(g1,g2) = 50
    c: Radius(g1) = 5
    c: Coincident(g3,g1)
    c: Coincident(g3,g2)
    c: Horizontal(g3)
    c: DistanceY(g-3,g1) = 3
FEATURE [PartDesign::Revolution] Revolution
  Angle = 360
  Angle2 = 60
  Axis = (1,-1e-16,0)
  Base = (-30,50,0)
  BaseFeature = -> Pad001
  Profile = -> Sketch
  ReferenceAxis = -> Sketch [Edge1]
  Refine = true
  Type = 0
FEATURE [PartDesign::PolarPattern] PolarPattern
  Angle = 360
  Axis = -> Sketch003 [N_Axis]
  BaseFeature = -> Revolution
  Mode = 0
  Occurrences = 3
  Offset = 120
  Originals = -> [Pad001,Revolution]
  Refine = true
FEATURE [PartDesign::Body] Body001  label="plate-skel"
  Group = -> [Sketch003,Pad001,Sketch,Revolution,PolarPattern]
  Origin = -> Origin002
  Tip = -> PolarPattern
FEATURE [Sketcher::SketchObject] Sketch005
  FullyConstrained = true
  MapMode = 5
  Support = -> [XY_Plane003]
  sketch-geometry (4):
    g0: LineSegment StartX=15 StartY=0 StartZ=0 EndX=15 EndY=50 EndZ=0
    g1: LineSegment StartX=15 StartY=50 StartZ=0 EndX=-15 EndY=50 EndZ=0
    g2: LineSegment StartX=-15 StartY=50 StartZ=0 EndX=-15 EndY=0 EndZ=0
    g3: LineSegment StartX=-15 StartY=0 StartZ=0 EndX=15 EndY=0 EndZ=0
  constraints (11):
    c: Coincident(g0,g1)
    c: Coincident(g1,g2)
    c: Coincident(g2,g3)
    c: Coincident(g3,g0)
    c: Vertical(g0)
    c: Vertical(g2)
    c: Horizontal(g1)
    c: PointOnObject(g0,g-1)
    c: Symmetric(g2,g0,g-2)
    c: DistanceX(g3,g3) = 30
    c: DistanceY(g0,g0) = 50
FEATURE [PartDesign::Pad] Pad002
  Direction = (0,0,1)
  Length = 6
  Length2 = 10
  Profile = -> Sketch005
  ReferenceAxis = -> Sketch005 [N_Axis]
  Type = 0
FEATURE [Sketcher::SketchObject] Sketch004
  ExternalGeometry = -> [Pad002]
  FullyConstrained = true
  MapMode = 5
  Support = -> [XY_Plane003]
  sketch-geometry (4):
    g0: LineSegment StartX=-29.9 StartY=50 StartZ=0 EndX=29.9 EndY=50 EndZ=0
    g1: ArcOfCircle CenterX=-25 CenterY=50 CenterZ=0 NormalX=0 NormalY=0 NormalZ=1 AngleXU=0 Radius=4.9 StartAngle=0.658897 EndAngle=3.14159
    g2: ArcOfCircle CenterX=25 CenterY=50 CenterZ=0 NormalX=0 NormalY=0 NormalZ=1 AngleXU=0 Radius=4.9 StartAngle=4e-16 EndAngle=2.4827
    g3: LineSegment StartX=-21.1257 StartY=53 StartZ=0 EndX=21.1257 EndY=53 EndZ=0
  constraints (12):
    c: Symmetric(g0,g0,g-2)
    c: PointOnObject(g-3,g0)
    c: PointOnObject(g1,g0)
    c: Coincident(g1,g0)
    c: Coincident(g2,g0)
    c: Symmetric(g1,g2,g-2)
    c: DistanceX(g1,g2) = 50
    c: Radius(g1) = 4.9
    c: Coincident(g3,g1)
    c: Coincident(g3,g2)
    c: Horizontal(g3)
    c: DistanceY(g-3,g1) = 3
FEATURE [PartDesign::Revolution] Revolution001
  Angle = 360
  Angle2 = 60
  Axis = (1,0,0)
  Base = (-29.9,50,0)
  BaseFeature = -> Pad002
  Profile = -> Sketch004
  ReferenceAxis = -> Sketch004 [Edge1]
  Refine = true
  Type = 0
FEATURE [PartDesign::PolarPattern] PolarPattern001
  Angle = 360
  Axis = -> Sketch005 [N_Axis]
  BaseFeature = -> Revolution001
  Mode = 0
  Occurrences = 3
  Offset = 120
  Originals = -> [Pad002,Revolution001]
  Refine = true
FEATURE [PartDesign::Chamfer] Chamfer
  Angle = 45
  Base = -> PolarPattern001 [Edge17,Edge44,Edge35]
  BaseFeature = -> PolarPattern001
  ChamferType = 0
  FlipDirection = false
  Refine = true
  Size = 2.4
  Size2 = 1
  SupportTransform = false
  UseAllEdges = false
FEATURE [Sketcher::SketchObject] Sketch006
  FullyConstrained = true
  MapMode = 5
  Placement = pos=(0,0,0) rot=(1,0,0;3.14159rad)
  Support = -> [Chamfer]
  sketch-geometry (7):
    g0: LineSegment StartX=25.9808 StartY=45 StartZ=0 EndX=-25.9808 EndY=45 EndZ=0
    g1: LineSegment StartX=-25.9808 StartY=45 StartZ=0 EndX=-51.9615 EndY=0 EndZ=0
    g2: LineSegment StartX=-51.9615 StartY=0 StartZ=0 EndX=-25.9808 EndY=-45 EndZ=0
    g3: LineSegment StartX=-25.9808 StartY=-45 StartZ=0 EndX=25.9808 EndY=-45 EndZ=0
    g4: LineSegment StartX=25.9808 StartY=-45 StartZ=0 EndX=51.9615 EndY=0 EndZ=0
    g5: LineSegment StartX=51.9615 StartY=0 StartZ=0 EndX=25.9808 EndY=45 EndZ=0
    g6: Circle CenterX=0 CenterY=0 CenterZ=0 NormalX=0 NormalY=0 NormalZ=1 AngleXU=0 Radius=51.9615
  constraints (16):
    c: Coincident(g0,g1)
    c: Coincident(g1,g2)
    c: Coincident(g2,g3)
    c: Coincident(g3,g4)
    c: Coincident(g4,g5)
    c: Coincident(g5,g0)
    c: Equal(g0, g1-g5) x5
    c: PointOnObject(g0,g6)
    c: PointOnObject(g1,g6)
    c: PointOnObject(g2,g6)
    c: PointOnObject(g3,g6)
    c: PointOnObject(g4,g6)
    c: PointOnObject(g5,g6)
    c: Coincident(g6,g-1)
    c: Horizontal(g0)
    c: DistanceY(g3,g0) = 90
FEATURE [PartDesign::Pocket] Pocket
  BaseFeature = -> Chamfer
  Direction = (0,0,1)
  Length = 3
  Length2 = 5
  Profile = -> Sketch006
  ReferenceAxis = -> Sketch006 [N_Axis]
  Refine = true
  Type = 0
FEATURE [Sketcher::SketchObject] Sketch007
  FullyConstrained = true
  MapMode = 5
  Placement = pos=(0,0,3) rot=(1,0,0;3.14159rad)
  Support = -> [Pocket]
  sketch-geometry (6):
    g0: Circle CenterX=-6.25 CenterY=-37.5 CenterZ=0 NormalX=0 NormalY=0 NormalZ=1 AngleXU=0 Radius=3.5
    g1: Circle CenterX=6.25 CenterY=-37.5 CenterZ=0 NormalX=0 NormalY=0 NormalZ=1 AngleXU=0 Radius=3.5
    g2: Circle CenterX=-6.25 CenterY=-25 CenterZ=0 NormalX=0 NormalY=0 NormalZ=1 AngleXU=0 Radius=3.5
    g3: Circle CenterX=6.25 CenterY=-25 CenterZ=0 NormalX=0 NormalY=0 NormalZ=1 AngleXU=0 Radius=3.5
    g4: Circle CenterX=6.25 CenterY=-12.5 CenterZ=0 NormalX=0 NormalY=0 NormalZ=1 AngleXU=0 Radius=3.5
    g5: Circle CenterX=-6.25 CenterY=-12.5 CenterZ=0 NormalX=0 NormalY=0 NormalZ=1 AngleXU=0 Radius=3.5
  constraints (15):
    c: Symmetric(g0,g1,g-2)
    c: Symmetric(g2,g3,g-2)
    c: DistanceX(g2,g3) = 12.5
    c: DistanceY(g1,g3) = 12.5
    c: Diameter(g3) = 7
    c: Equal(g2,g3)
    c: Equal(g0,g1)
    c: DistanceY(g3,g-1) = 25
    c: Vertical(g3,g1)
    c: Equal(g0,g2)
    c: Symmetric(g5,g4,g-2)
    c: Vertical(g2,g5)
    c: DistanceY(g3,g4) = 12.5
    c: Equal(g5,g2)
    c: Equal(g4,g5)
FEATURE [PartDesign::Pocket] Pocket001
  BaseFeature = -> Pocket
  Direction = (0,0,1)
  Length = 5
  Length2 = 5
  Profile = -> Sketch007
  ReferenceAxis = -> Sketch007 [N_Axis]
  Refine = true
  Type = 1
FEATURE [PartDesign::PolarPattern] PolarPattern002
  Angle = 360
  Axis = -> Z_Axis003
  BaseFeature = -> Pocket001
  Mode = 0
  Occurrences = 3
  Offset = 120
  Originals = -> [Pocket001]
  Refine = true
FEATURE [PartDesign::Chamfer] Chamfer001
  Angle = 45
  Base = -> PolarPattern002 [Edge68,Edge120,Edge121]
  BaseFeature = -> PolarPattern002
  ChamferType = 0
  FlipDirection = false
  Refine = true
  Size = 1
  Size2 = 1
  SupportTransform = false
  UseAllEdges = false
FEATURE [PartDesign::Body] Body002  label="plate-0"
  Group = -> [Sketch005,Pad002,Sketch004,Revolution001,PolarPattern001,Chamfer,Sketch006,Pocket,Sketch007,Pocket001,PolarPattern002,Chamfer001]
  Origin = -> Origin003
  Tip = -> Chamfer001
FEATURE [App::Part] Part  label="plate"
  Group = -> [Body001,Body002]
  Origin = -> Origin001
PROVENANCE & LICENSES
A FreeCAD (.FCStd) document from a public repository crawl; recipes are the document's own serialized feature recipes (and, for linked parts, companion documents' recipes).
License: lgpl-3.0.
